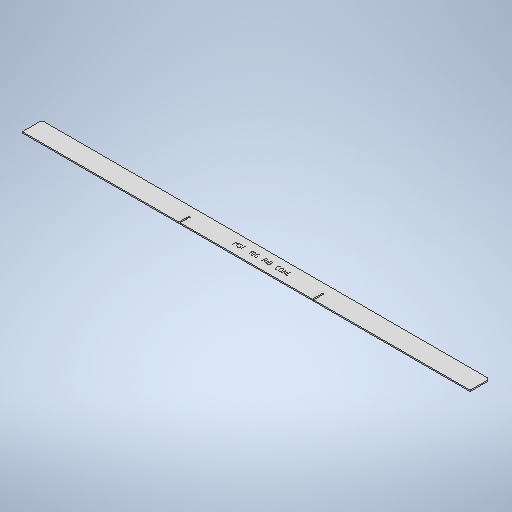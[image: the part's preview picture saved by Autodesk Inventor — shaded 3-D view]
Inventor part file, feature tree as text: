
AUTODESK INVENTOR PART (.ipt)
format: ipt  version: 2025 (Build 290162010, 162A)  size: 418,816 bytes
history: native  units: mm
features: other x5, sketch x4, extrude x2, sheet_metal_op x1, projected_geometry x1
ambient origin geometry x8: Origin, YZ Plane, XZ Plane, XY Plane, X Axis, Y Axis, Z Axis, Center Point
bodies: Body1 (feature_tree)
feature tree (13):
  sheet_metal_op  "Face1"
  extrude  "Extrusion2"  Depth=1200.0mm
  extrude  "Extrusion3"  Depth=50.0mm
  other  "Mark1"
  other  "Corner Chamfer1"
  other  "A-Side Definition"
  sketch  "Sketch1"  dims[d18=50.0mm d19=1200.0mm]
  other  "Plate2"
  sketch  "Sketch3"  dims[d20=3.0mm d25=50.0mm]
  sketch  "Sketch4"  dims[d26=50.0mm]
  projected_geometry  "Projected Loop1"
  sketch  "Sketch5"  dims[d28=3.1mm d29=26.0mm d30=0.0mm d31=0.0mm d39=12.217305mm d40=35.0mm d45=25.0mm d46=25.0mm d47=0.0mm d48=0.0mm d49=6.0mm d50=6.0mm d51=45.0deg d52=340.0mm]
  other  "Definition1"
